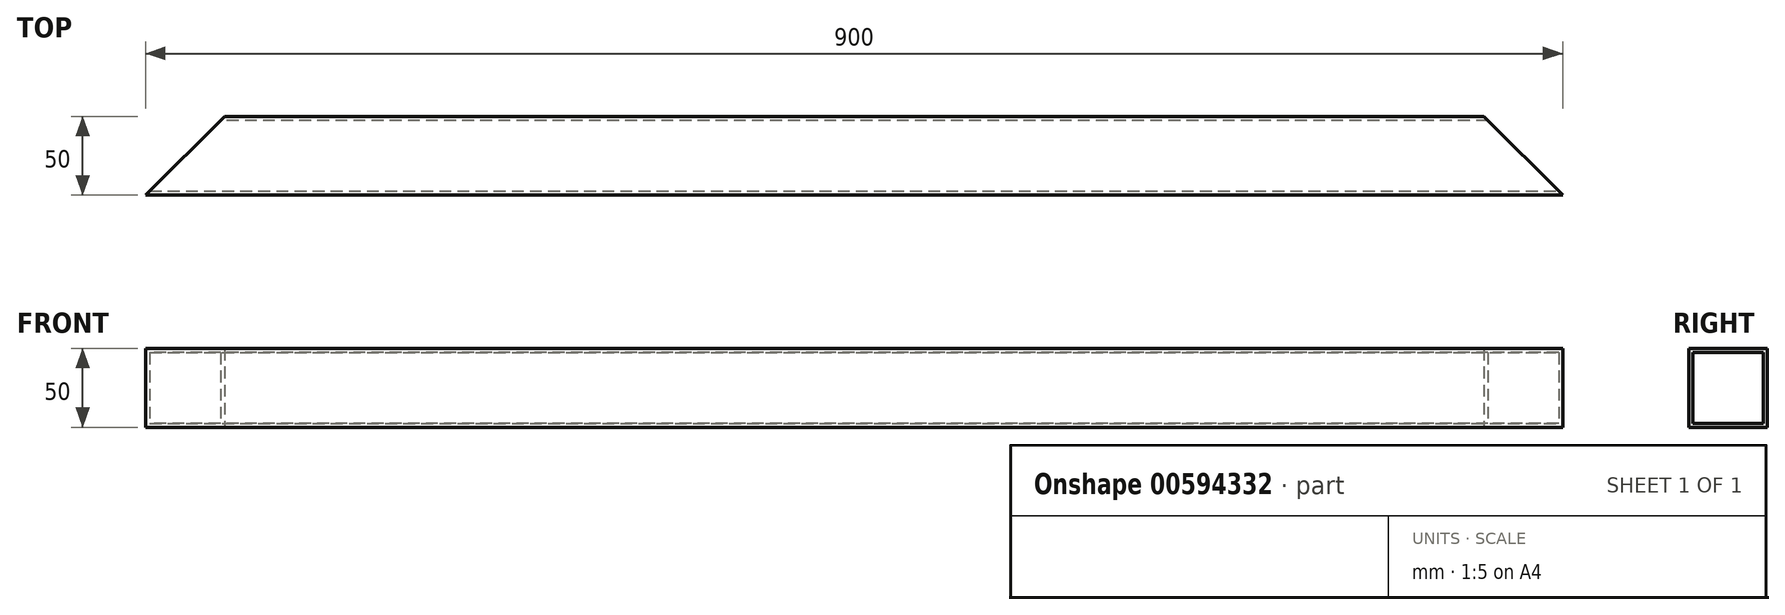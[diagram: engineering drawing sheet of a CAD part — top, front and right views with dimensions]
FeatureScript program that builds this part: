
annotation { "Feature Type Name" : "Feature", "Feature Type Description" : "" }
export const myFeature = defineFeature(function(context is Context, id is Id, definition is map)
    precondition{}
    {
        {
            var Q0;
            Q0=qCreatedBy(makeId("Top.planeOp"),FACE);
            var sketch = newSketch(context, id + "F0", { "sketchPlane" : qUnion([Q0])});
            skLineSegment(sketch, "E0", {"start": v(0, 0) * mm, "end": v(0, -50) * mm});
            skLineSegment(sketch, "E1", {"start": v(0, -50) * mm, "end": v(450, -50) * mm});
            skLineSegment(sketch, "E2", {"start": v(450, -50) * mm, "end": v(400, 0) * mm});
            skLineSegment(sketch, "E3", {"start": v(400, 0) * mm, "end": v(0, 0) * mm});
            skLineSegment(sketch, "E4", {"start": v(-400, 0) * mm, "end": v(-450, -50) * mm});
            skLineSegment(sketch, "E5", {"start": v(-450, -50) * mm, "end": v(0, -50) * mm});
            skLineSegment(sketch, "E6", {"start": v(0, 0) * mm, "end": v(-400, 0) * mm});
            skSolve(sketch);
        }
        {
            var Q0;
            Q0=makeQuery(id+"F0.imprint","IMPRINT",FACE,{"disambiguationData":[TD([[makeQuery(id+"F0.imprint","IMPRINT",EDGE,{"derivedFrom":sQuery(id+"F0.wireOp",EDGE,"E0")}),1.0]])]});
            var Q1;
            Q1=makeQuery(id+"F0.imprint","IMPRINT",FACE,{"disambiguationData":[TD([[makeQuery(id+"F0.imprint","IMPRINT",EDGE,{"derivedFrom":sQuery(id+"F0.wireOp",EDGE,"E0")}),-1.0]])]});
            extrude(context, id + "F1", {"entities" : qUnion([Q0, Q1]), "depth" : 50 * mm, "offsetDistance" : 25.4 * mm});
        }
        {
            var Q0;
            Q0=makeQuery(id+"F1.opExtrude","SWEPT_FACE",FACE,{"disambiguationData":[OSD([sQuery(id+"F0.wireOp",EDGE,"E2")])]});
            var Q1;
            Q1=makeQuery(id+"F1.opExtrude","SWEPT_FACE",FACE,{"disambiguationData":[OSD([sQuery(id+"F0.wireOp",EDGE,"E4")])]});
            shell(context, id + "F2", {"entities" : qUnion([Q0, Q1]), "thickness" : 2.54 * mm});
        }
    });
